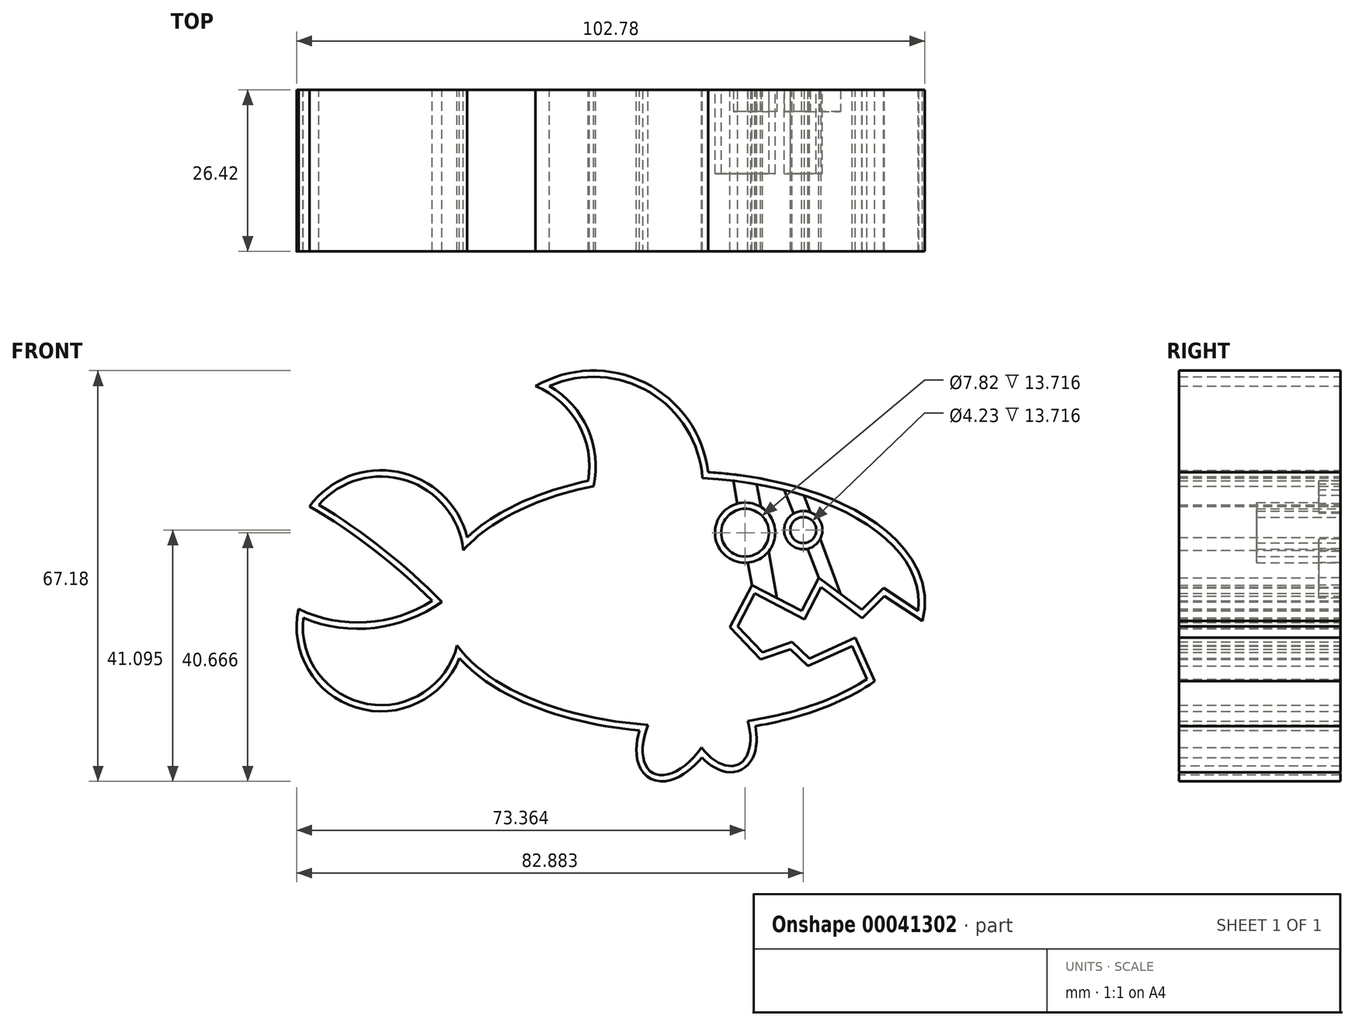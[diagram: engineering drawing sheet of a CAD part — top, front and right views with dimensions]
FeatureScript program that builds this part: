
annotation { "Feature Type Name" : "Feature", "Feature Type Description" : "" }
export const myFeature = defineFeature(function(context is Context, id is Id, definition is map)
    precondition{}
    {
        {
            var Q0;
            Q0=qCreatedBy(makeId("Front.planeOp"),FACE);
            var sketch = newSketch(context, id + "F0", { "sketchPlane" : qUnion([Q0])});
            skEllipticalArc(sketch, "E0", {});
            skEllipticalArc(sketch, "E1", {});
            skEllipticalArc(sketch, "E2", {});
            skLineSegment(sketch, "E3", {"start": v(-3.87, 19.18) * mm, "end": v(-9.52, 22.9) * mm});
            skLineSegment(sketch, "E4", {"start": v(-9.52, 22.9) * mm, "end": v(-13.09, 19.34) * mm});
            skLineSegment(sketch, "E5", {"start": v(-13.09, 19.34) * mm, "end": v(-20.09, 24.57) * mm});
            skLineSegment(sketch, "E6", {"start": v(-20.09, 24.57) * mm, "end": v(-22.88, 19.16) * mm});
            skLineSegment(sketch, "E7", {"start": v(-22.88, 19.16) * mm, "end": v(-31.05, 23.38) * mm});
            skLineSegment(sketch, "E8", {"start": v(-31.05, 23.38) * mm, "end": v(-34.63, 16.48) * mm});
            skLineSegment(sketch, "E9", {"start": v(-34.63, 16.48) * mm, "end": v(-29.63, 11.24) * mm});
            skLineSegment(sketch, "E10", {"start": v(-29.63, 11.24) * mm, "end": v(-24.76, 12.9) * mm});
            skLineSegment(sketch, "E11", {"start": v(-24.76, 12.9) * mm, "end": v(-21.87, 10.18) * mm});
            skLineSegment(sketch, "E12", {"start": v(-21.87, 10.18) * mm, "end": v(-14.64, 13.42) * mm});
            skLineSegment(sketch, "E13", {"start": v(-14.64, 13.42) * mm, "end": v(-12.21, 8.02) * mm});
            skArc(sketch, "E14", {"start": v(-64.18, 55.94) * mm, "mid": v(-47.76, 54.9) * mm, "end": v(-39.14, 40.89) * mm});
            skArc(sketch, "E15", {"start": v(-56.97, 39.58) * mm, "mid": v(-57.91, 48.93) * mm, "end": v(-64.18, 55.94) * mm});
            skArc(sketch, "E16", {"start": v(-78.26, 29.08) * mm, "mid": v(-87.64, 40.52) * mm, "end": v(-101.9, 36.54) * mm});
            skArc(sketch, "E17", {"start": v(-79.29, 13.52) * mm, "mid": v(-93.96, 3.96) * mm, "end": v(-104.43, 18) * mm});
            skArc(sketch, "E18", {"start": v(-104.43, 18) * mm, "mid": v(-92.76, 16.4) * mm, "end": v(-81.77, 20.65) * mm});
            skArc(sketch, "E19", {"start": v(-81.77, 20.65) * mm, "mid": v(-91.33, 29.23) * mm, "end": v(-101.9, 36.54) * mm});
            skEllipticalArc(sketch, "E20.trimOffspring", {});
            skEllipticalArc(sketch, "E21.trimOffspring", {});
            skEllipticalArc(sketch, "E22.trimOffspring", {});
            skPoint(sketch, "E23.rect.middle", {"position": v(-51.99, 21.31) * mm});
            skCircle(sketch, "E24", {"center": v(-32.17, 31.96) * mm, "radius": 4.93 * mm});
            skCircle(sketch, "E25", {"center": v(-22.65, 32.38) * mm, "radius": 3.13 * mm});
            skLineSegment(sketch, "E26", {"start": v(-34.08, 40.47) * mm, "end": v(-31.05, 23.38) * mm});
            skLineSegment(sketch, "E27", {"start": v(-26.97, 21.27) * mm, "end": v(-30.27, 39.9) * mm});
            skLineSegment(sketch, "E28", {"start": v(-25.73, 38.94) * mm, "end": v(-20.09, 24.57) * mm});
            skLineSegment(sketch, "E29", {"start": v(-22.5, 38.02) * mm, "end": v(-16.59, 21.95) * mm});
            const initialGuessF0  = {"E0": [-0.04276583048879895, 0.020653425790234083, 1, 0, 0.03900148710716327, 0.020322355287553013, 1.9434975103677201, 2.714200347047995], "E1": [-0.04276583048879896, 0.00033107050268106966, -0.5116268366018603, -0.8592077630403332, 0.008891221735082715, 0.004842302721957304, 5.002614857527723, 1.432086669458521], "E2": [-0.036566919295762265, 0.001142065546469207, 0.4154602851956659, -0.9096113188747906, 0.007806887266890362, 0.004562561181037419, 5.079984399451636, 1.3126795490912948], "E20.trimOffspring": [-0.04276583048879895, 0.020653425790234083, 1, 0, 0.03900148710716327, 0.020322355287553013, 6.210618095516672, 1.477710423523917], "E21.trimOffspring": [-0.04276583048879895, 0.020653425790234083, 1, 0, 0.03900148710716327, 0.020322355287553013, 3.5002520530126784, 4.57637711479995], "E22.trimOffspring": [-0.04276583048879895, 0.020653425790234083, 1, 0, 0.03900148710716327, 0.020322355287553013, 4.9993653097453095, 5.612392853776827]};
            skSetInitialGuess(sketch, initialGuessF0);
            skSolve(sketch);
        }
        {
            var Q0;
            Q0=makeQuery(id+"F0.imprint","IMPRINT",FACE,{"disambiguationData":[TD([[makeQuery(id+"F0.imprint","IMPRINT",EDGE,{"derivedFrom":sQuery(id+"F0.wireOp",EDGE,"E0")}),1.0]])]});
            var Q1;
            {var subQ8=sQuery(id+"F0.wireOp",EDGE,"E3");Q1=makeQuery(id+"F0.imprint","IMPRINT",FACE,{"disambiguationData":[TD([[makeQuery(id+"F0.imprint","IMPRINT",EDGE,{"derivedFrom":subQ8}),-1.0]])]});}
            var Q2;
            {var subQ10=sQuery(id+"F0.wireOp",EDGE,"E6");Q2=makeQuery(id+"F0.imprint","IMPRINT",FACE,{"disambiguationData":[TD([[makeQuery(id+"F0.imprint","IMPRINT",EDGE,{"derivedFrom":subQ10}),-1.0]])]});}
            var Q3;
            {var subQ0=sQuery(id+"F0.wireOp",EDGE,"E26");var subQ1=sQuery(id+"F0.wireOp",EDGE,"E24");var subQ2=makeQuery(id+"F0.imprint","INTERSECT",VERTEX,{"disambiguationData":[OD(1.0)],"derivedFrom":[subQ1,subQ0]});Q3=makeQuery(id+"F0.imprint","IMPRINT",FACE,{"disambiguationData":[TD([[makeQuery(id+"F0.imprint","IMPRINT",EDGE,{"disambiguationData":[TD([[subQ2,-1.0]])],"derivedFrom":subQ1}),-1.0]])]});}
            var Q4;
            {var subQ0=sQuery(id+"F0.wireOp",EDGE,"E26");var subQ3=sQuery(id+"F0.wireOp",EDGE,"E20.trimOffspring");var subQ4=makeQuery(id+"F0.imprint","INTERSECT",VERTEX,{"derivedFrom":[subQ3,subQ0]});Q4=makeQuery(id+"F0.imprint","IMPRINT",FACE,{"disambiguationData":[TD([[makeQuery(id+"F0.imprint","IMPRINT",EDGE,{"disambiguationData":[TD([[subQ4,1.0]])],"derivedFrom":subQ3}),1.0]])]});}
            var Q5;
            {var subQ0=sQuery(id+"F0.wireOp",EDGE,"E29");var subQ3=sQuery(id+"F0.wireOp",EDGE,"E20.trimOffspring");var subQ4=makeQuery(id+"F0.imprint","INTERSECT",VERTEX,{"derivedFrom":[subQ3,subQ0]});Q5=makeQuery(id+"F0.imprint","IMPRINT",FACE,{"disambiguationData":[TD([[makeQuery(id+"F0.imprint","IMPRINT",EDGE,{"disambiguationData":[TD([[subQ4,-1.0]])],"derivedFrom":subQ3}),1.0]])]});}
            var Q6;
            {var subQ1=sQuery(id+"F0.wireOp",EDGE,"E25");var subQ5=sQuery(id+"F0.wireOp",EDGE,"E28");var subQ6=makeQuery(id+"F0.imprint","INTERSECT",VERTEX,{"disambiguationData":[OD(1.0)],"derivedFrom":[subQ1,subQ5]});Q6=makeQuery(id+"F0.imprint","IMPRINT",FACE,{"disambiguationData":[TD([[makeQuery(id+"F0.imprint","IMPRINT",EDGE,{"disambiguationData":[TD([[subQ6,-1.0]])],"derivedFrom":subQ1}),-1.0]])]});}
            extrude(context, id + "F1", {"entities" : qUnion([Q0, Q1, Q2, Q3, Q4, Q5, Q6]), "depth" : 25.4 * mm});
        }
        {
            var Q0;
            Q0=makeQuery(id+"F1.opExtrude","CAP_FACE",FACE,{"disambiguationData":[OSD([sQuery(id+"F0.wireOp",EDGE,"E0"),sQuery(id+"F0.wireOp",EDGE,"E1"),sQuery(id+"F0.wireOp",EDGE,"E2"),sQuery(id+"F0.wireOp",EDGE,"E3"),sQuery(id+"F0.wireOp",EDGE,"E4"),sQuery(id+"F0.wireOp",EDGE,"E5"),sQuery(id+"F0.wireOp",EDGE,"E6"),sQuery(id+"F0.wireOp",EDGE,"E7"),sQuery(id+"F0.wireOp",EDGE,"E8"),sQuery(id+"F0.wireOp",EDGE,"E9"),sQuery(id+"F0.wireOp",EDGE,"E10"),sQuery(id+"F0.wireOp",EDGE,"E11"),sQuery(id+"F0.wireOp",EDGE,"E12"),sQuery(id+"F0.wireOp",EDGE,"E13"),sQuery(id+"F0.wireOp",EDGE,"E14"),sQuery(id+"F0.wireOp",EDGE,"E15"),sQuery(id+"F0.wireOp",EDGE,"E16"),sQuery(id+"F0.wireOp",EDGE,"E17"),sQuery(id+"F0.wireOp",EDGE,"E18"),sQuery(id+"F0.wireOp",EDGE,"E19"),sQuery(id+"F0.wireOp",EDGE,"E20.trimOffspring"),sQuery(id+"F0.wireOp",EDGE,"E21.trimOffspring"),sQuery(id+"F0.wireOp",EDGE,"E22.trimOffspring"),sQuery(id+"F0.wireOp",EDGE,"E24"),sQuery(id+"F0.wireOp",EDGE,"E25")])],"isStart":false});
            shell(context, id + "F2", {"entities" : qUnion([Q0]), "thickness" : 1.02 * mm, "oppositeDirection" : true});
        }
        {
            var Q0;
            Q0=makeQuery(id+"F0.imprint","IMPRINT",FACE,{"disambiguationData":[TD([[makeQuery(id+"F0.imprint","IMPRINT",EDGE,{"derivedFrom":sQuery(id+"F0.wireOp",EDGE,"E0")}),1.0]])]});
            var Q1;
            {var subQ10=sQuery(id+"F0.wireOp",EDGE,"E6");Q1=makeQuery(id+"F0.imprint","IMPRINT",FACE,{"disambiguationData":[TD([[makeQuery(id+"F0.imprint","IMPRINT",EDGE,{"derivedFrom":subQ10}),-1.0]])]});}
            var Q2;
            {var subQ8=sQuery(id+"F0.wireOp",EDGE,"E3");Q2=makeQuery(id+"F0.imprint","IMPRINT",FACE,{"disambiguationData":[TD([[makeQuery(id+"F0.imprint","IMPRINT",EDGE,{"derivedFrom":subQ8}),-1.0]])]});}
            extrude(context, id + "F3", {"entities" : qUnion([Q0, Q1, Q2]), "operationType" : NewBodyOperationType.REMOVE, "oppositeDirection" : true, "depth" : 25.4 * mm});
        }
        {
            var Q0;
            {var subQ0=sQuery(id+"F0.wireOp",EDGE,"E0");var subQ1=sQuery(id+"F0.wireOp",EDGE,"E1");var subQ2=sQuery(id+"F0.wireOp",EDGE,"E2");var subQ3=sQuery(id+"F0.wireOp",EDGE,"E3");var subQ4=sQuery(id+"F0.wireOp",EDGE,"E4");var subQ5=sQuery(id+"F0.wireOp",EDGE,"E5");var subQ6=sQuery(id+"F0.wireOp",EDGE,"E6");var subQ7=sQuery(id+"F0.wireOp",EDGE,"E7");var subQ8=sQuery(id+"F0.wireOp",EDGE,"E8");var subQ9=sQuery(id+"F0.wireOp",EDGE,"E9");var subQ10=sQuery(id+"F0.wireOp",EDGE,"E10");var subQ11=sQuery(id+"F0.wireOp",EDGE,"E11");var subQ12=sQuery(id+"F0.wireOp",EDGE,"E12");var subQ13=sQuery(id+"F0.wireOp",EDGE,"E13");var subQ14=sQuery(id+"F0.wireOp",EDGE,"E14");var subQ15=sQuery(id+"F0.wireOp",EDGE,"E15");var subQ16=sQuery(id+"F0.wireOp",EDGE,"E16");var subQ17=sQuery(id+"F0.wireOp",EDGE,"E17");var subQ18=sQuery(id+"F0.wireOp",EDGE,"E18");var subQ19=sQuery(id+"F0.wireOp",EDGE,"E19");var subQ20=sQuery(id+"F0.wireOp",EDGE,"E20.trimOffspring");var subQ21=sQuery(id+"F0.wireOp",EDGE,"E21.trimOffspring");var subQ22=sQuery(id+"F0.wireOp",EDGE,"E22.trimOffspring");var subQ23=sQuery(id+"F0.wireOp",EDGE,"E24");var subQ24=sQuery(id+"F0.wireOp",EDGE,"E25");Q0=makeQuery(id+"F2.opShell","OFFSET_FACE",FACE,{"disambiguationData":[OSD([subQ0,subQ1,subQ2,subQ3,subQ4,subQ5,subQ6,subQ7,subQ8,subQ9,subQ10,subQ11,subQ12,subQ13,subQ14,subQ15,subQ16,subQ17,subQ18,subQ19,subQ20,subQ21,subQ22,subQ23,subQ24]),TDD([makeQuery(id+"F1.opExtrude","CAP_FACE",FACE,{"disambiguationData":[OSD([subQ0,subQ1,subQ2,subQ3,subQ4,subQ5,subQ6,subQ7,subQ8,subQ9,subQ10,subQ11,subQ12,subQ13,subQ14,subQ15,subQ16,subQ17,subQ18,subQ19,subQ20,subQ21,subQ22,subQ23,subQ24])],"isStart":false})]),OD(1.0)]});}
            var Q1;
            Q1=makeQuery(id+"F1.opExtrude","CAP_FACE",FACE,{"disambiguationData":[OSD([sQuery(id+"F0.wireOp",EDGE,"E0"),sQuery(id+"F0.wireOp",EDGE,"E1"),sQuery(id+"F0.wireOp",EDGE,"E2"),sQuery(id+"F0.wireOp",EDGE,"E3"),sQuery(id+"F0.wireOp",EDGE,"E4"),sQuery(id+"F0.wireOp",EDGE,"E5"),sQuery(id+"F0.wireOp",EDGE,"E6"),sQuery(id+"F0.wireOp",EDGE,"E7"),sQuery(id+"F0.wireOp",EDGE,"E8"),sQuery(id+"F0.wireOp",EDGE,"E9"),sQuery(id+"F0.wireOp",EDGE,"E10"),sQuery(id+"F0.wireOp",EDGE,"E11"),sQuery(id+"F0.wireOp",EDGE,"E12"),sQuery(id+"F0.wireOp",EDGE,"E13"),sQuery(id+"F0.wireOp",EDGE,"E14"),sQuery(id+"F0.wireOp",EDGE,"E15"),sQuery(id+"F0.wireOp",EDGE,"E16"),sQuery(id+"F0.wireOp",EDGE,"E17"),sQuery(id+"F0.wireOp",EDGE,"E18"),sQuery(id+"F0.wireOp",EDGE,"E19"),sQuery(id+"F0.wireOp",EDGE,"E20.trimOffspring"),sQuery(id+"F0.wireOp",EDGE,"E21.trimOffspring"),sQuery(id+"F0.wireOp",EDGE,"E22.trimOffspring"),sQuery(id+"F0.wireOp",EDGE,"E24"),sQuery(id+"F0.wireOp",EDGE,"E25")])],"isStart":false});
            extrude(context, id + "F4", {"entities" : qUnion([Q0, Q1]), "operationType" : NewBodyOperationType.REMOVE, "oppositeDirection" : true, "depth" : 12.7 * mm});
        }
        {
            var Q0;
            {var subQ0=sQuery(id+"F0.wireOp",EDGE,"E26");var subQ3=sQuery(id+"F0.wireOp",EDGE,"E20.trimOffspring");var subQ4=makeQuery(id+"F0.imprint","INTERSECT",VERTEX,{"derivedFrom":[subQ3,subQ0]});Q0=makeQuery(id+"F0.imprint","IMPRINT",FACE,{"disambiguationData":[TD([[makeQuery(id+"F0.imprint","IMPRINT",EDGE,{"disambiguationData":[TD([[subQ4,1.0]])],"derivedFrom":subQ3}),1.0]])]});}
            var Q1;
            {var subQ0=sQuery(id+"F0.wireOp",EDGE,"E29");var subQ3=sQuery(id+"F0.wireOp",EDGE,"E20.trimOffspring");var subQ4=makeQuery(id+"F0.imprint","INTERSECT",VERTEX,{"derivedFrom":[subQ3,subQ0]});Q1=makeQuery(id+"F0.imprint","IMPRINT",FACE,{"disambiguationData":[TD([[makeQuery(id+"F0.imprint","IMPRINT",EDGE,{"disambiguationData":[TD([[subQ4,-1.0]])],"derivedFrom":subQ3}),1.0]])]});}
            var Q2;
            {var subQ0=sQuery(id+"F0.wireOp",EDGE,"E26");var subQ1=sQuery(id+"F0.wireOp",EDGE,"E24");var subQ2=makeQuery(id+"F0.imprint","INTERSECT",VERTEX,{"disambiguationData":[OD(1.0)],"derivedFrom":[subQ1,subQ0]});Q2=makeQuery(id+"F0.imprint","IMPRINT",FACE,{"disambiguationData":[TD([[makeQuery(id+"F0.imprint","IMPRINT",EDGE,{"disambiguationData":[TD([[subQ2,-1.0]])],"derivedFrom":subQ1}),-1.0]])]});}
            var Q3;
            {var subQ1=sQuery(id+"F0.wireOp",EDGE,"E25");var subQ5=sQuery(id+"F0.wireOp",EDGE,"E28");var subQ6=makeQuery(id+"F0.imprint","INTERSECT",VERTEX,{"disambiguationData":[OD(1.0)],"derivedFrom":[subQ1,subQ5]});Q3=makeQuery(id+"F0.imprint","IMPRINT",FACE,{"disambiguationData":[TD([[makeQuery(id+"F0.imprint","IMPRINT",EDGE,{"disambiguationData":[TD([[subQ6,-1.0]])],"derivedFrom":subQ1}),-1.0]])]});}
            extrude(context, id + "F5", {"entities" : qUnion([Q0, Q1, Q2, Q3]), "operationType" : NewBodyOperationType.ADD, "depth" : 2.54 * mm});
        }
    });
